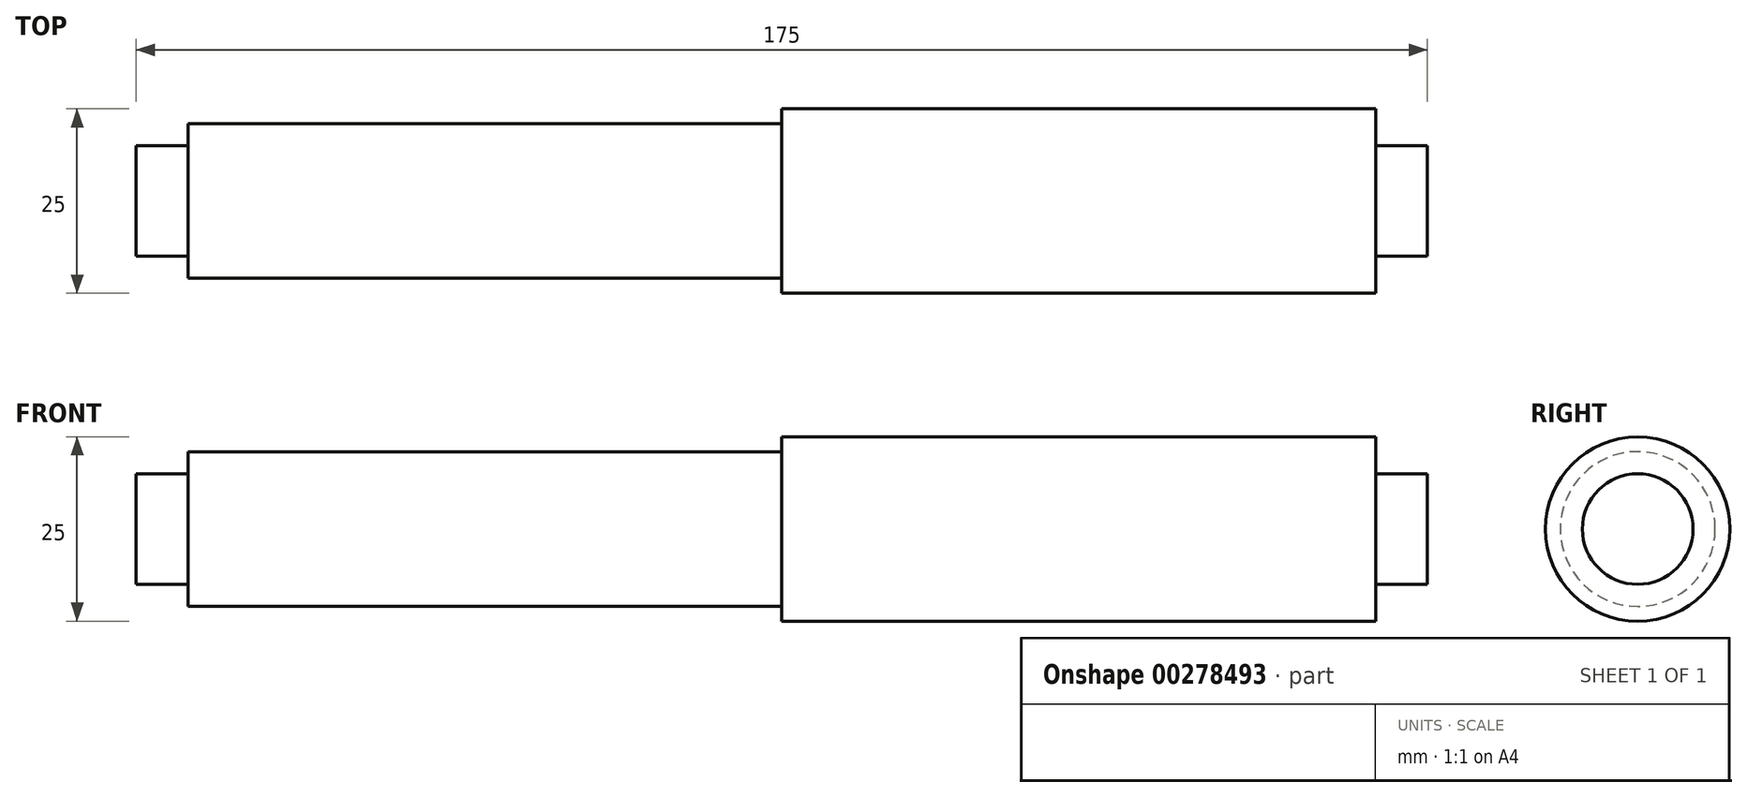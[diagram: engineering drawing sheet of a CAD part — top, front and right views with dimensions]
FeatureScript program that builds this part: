
annotation { "Feature Type Name" : "Feature", "Feature Type Description" : "" }
export const myFeature = defineFeature(function(context is Context, id is Id, definition is map)
    precondition{}
    {
        {
            var Q0;
            Q0=qCreatedBy(makeId("Front.planeOp"),FACE);
            var sketch = newSketch(context, id + "F0", { "sketchPlane" : qUnion([Q0])});
            skLineSegment(sketch, "E0", {"start": v(-87.5, 0) * mm, "end": v(-87.5, 7.5) * mm});
            skLineSegment(sketch, "E1", {"start": v(-87.5, 7.5) * mm, "end": v(-80.5, 7.5) * mm});
            skLineSegment(sketch, "E2", {"start": v(-80.5, 7.5) * mm, "end": v(-80.5, 10.5) * mm});
            skLineSegment(sketch, "E3", {"start": v(-80.5, 10.5) * mm, "end": v(0, 10.5) * mm});
            skLineSegment(sketch, "E4", {"start": v(0, 12.5) * mm, "end": v(80.5, 12.5) * mm});
            skLineSegment(sketch, "E5", {"start": v(80.5, 12.5) * mm, "end": v(80.5, 7.5) * mm});
            skLineSegment(sketch, "E6", {"start": v(80.5, 7.5) * mm, "end": v(87.5, 7.5) * mm});
            skLineSegment(sketch, "E7", {"start": v(87.5, 7.5) * mm, "end": v(87.5, 0) * mm});
            skLineSegment(sketch, "E8", {"start": v(-87.5, 0) * mm, "end": v(87.5, 0) * mm});
            skLineSegment(sketch, "E9", {"start": v(0, 12.5) * mm, "end": v(0, 10.5) * mm});
            skSolve(sketch);
        }
        {
            var Q0;
            Q0=makeQuery(id+"F0.imprint","IMPRINT",FACE,{"disambiguationData":[TD([[makeQuery(id+"F0.imprint","IMPRINT",EDGE,{"derivedFrom":sQuery(id+"F0.wireOp",EDGE,"E0")}),-1.0]])]});
            var Q1;
            Q1=sQuery(id+"F0.wireOp",EDGE,"E8");
            revolve(context, id + "F1", {"entities" : qUnion([Q0]), "axis" : qUnion([Q1]), "revolveType" : RevolveType.FULL});
        }
    });
